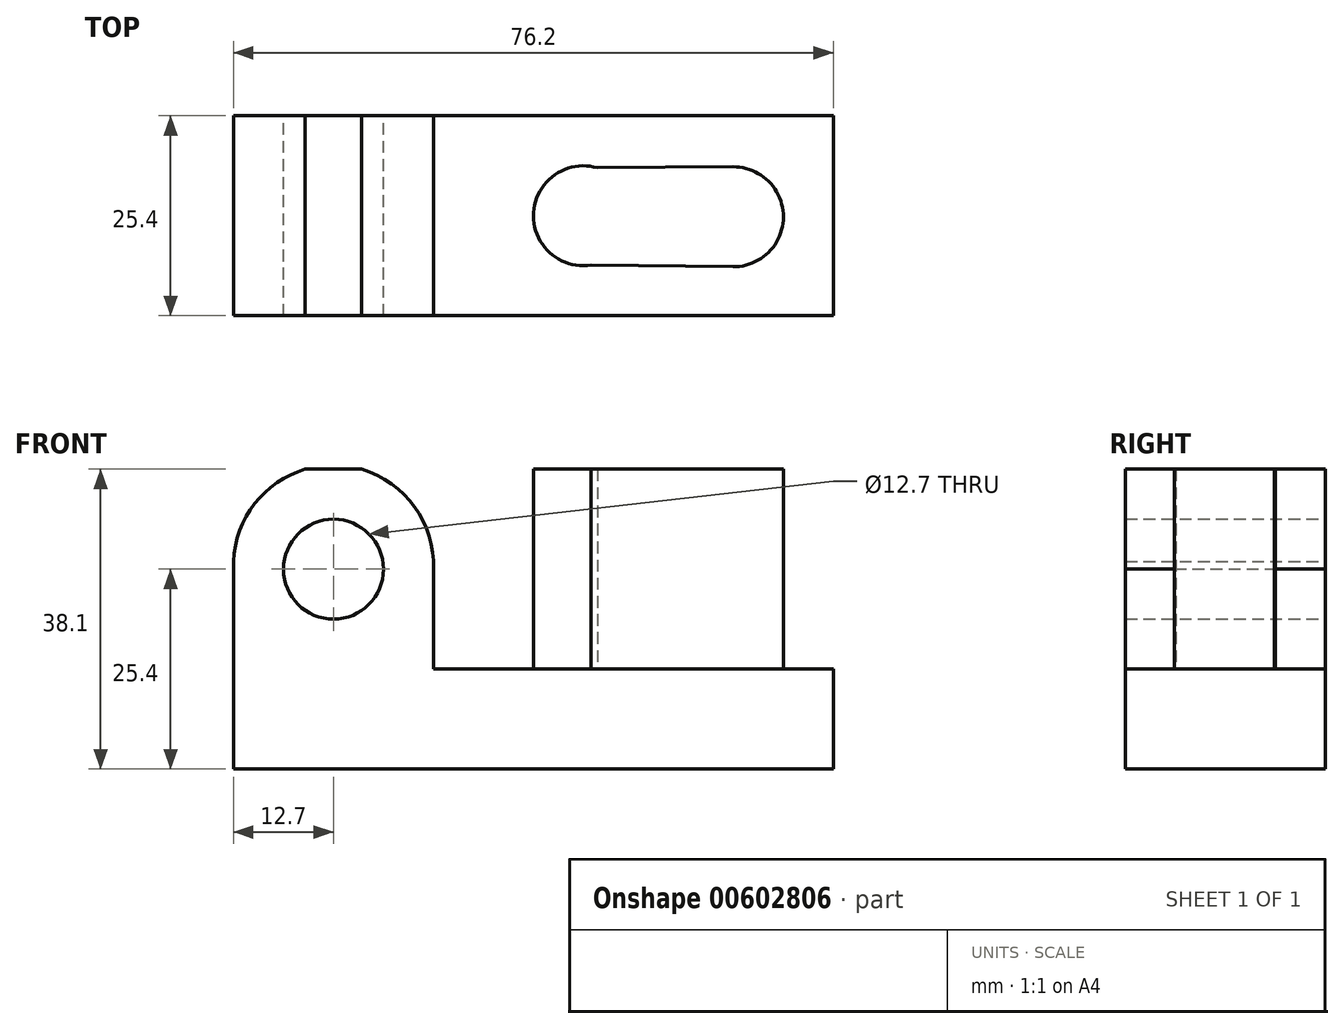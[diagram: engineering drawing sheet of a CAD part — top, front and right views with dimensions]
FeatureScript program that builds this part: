
annotation { "Feature Type Name" : "Feature", "Feature Type Description" : "" }
export const myFeature = defineFeature(function(context is Context, id is Id, definition is map)
    precondition{}
    {
        {
            var Q0;
            Q0=qCreatedBy(makeId("Front.planeOp"),FACE);
            var sketch = newSketch(context, id + "F0", { "sketchPlane" : qUnion([Q0])});
            skLineSegment(sketch, "E0", {"start": v(0, 0) * mm, "end": v(0, 38.1) * mm});
            skLineSegment(sketch, "E1", {"start": v(0, 38.1) * mm, "end": v(25.4, 38.1) * mm});
            skLineSegment(sketch, "E2", {"start": v(25.4, 38.1) * mm, "end": v(25.4, 12.7) * mm});
            skLineSegment(sketch, "E3", {"start": v(25.4, 12.7) * mm, "end": v(76.2, 12.7) * mm});
            skLineSegment(sketch, "E4", {"start": v(76.2, 12.7) * mm, "end": v(76.2, 0) * mm});
            skLineSegment(sketch, "E5", {"start": v(0, 0) * mm, "end": v(76.2, 0) * mm});
            skCircle(sketch, "E6", {"center": v(12.7, 25.4) * mm, "radius": 6.35 * mm});
            skPoint(sketch, "E6.centerSnap0", {"position": v(12.7, 38.1) * mm});
            skArc(sketch, "E7", {"start": v(25.4, 25.4) * mm, "mid": v(12.7, 38.61) * mm, "end": v(0, 25.4) * mm});
            skPoint(sketch, "E7.endSnap0", {"position": v(25.4, 25.4) * mm});
            skSolve(sketch);
        }
        {
            var Q0;
            {var subQ0=sQuery(id+"F0.wireOp",EDGE,"E7");var subQ1=sQuery(id+"F0.wireOp",EDGE,"E0");var subQ2=makeQuery(id+"F0.imprint","INTERSECT",VERTEX,{"disambiguationData":[OD(0.0)],"derivedFrom":[subQ1,subQ0]});Q0=makeQuery(id+"F0.imprint","IMPRINT",FACE,{"disambiguationData":[TD([[makeQuery(id+"F0.imprint","IMPRINT",EDGE,{"disambiguationData":[TD([[subQ2,-1.0]])],"derivedFrom":subQ1}),1.0]])]});}
            var Q1;
            {var subQ0=sQuery(id+"F0.wireOp",EDGE,"E7");var subQ1=sQuery(id+"F0.wireOp",EDGE,"E1");var subQ2=makeQuery(id+"F0.imprint","INTERSECT",VERTEX,{"disambiguationData":[OD(0.0)],"derivedFrom":[subQ1,subQ0]});Q1=makeQuery(id+"F0.imprint","IMPRINT",FACE,{"disambiguationData":[TD([[makeQuery(id+"F0.imprint","IMPRINT",EDGE,{"disambiguationData":[TD([[subQ2,-1.0]])],"derivedFrom":subQ1}),1.0]])]});}
            var Q2;
            {var subQ0=sQuery(id+"F0.wireOp",EDGE,"E7");var subQ1=sQuery(id+"F0.wireOp",EDGE,"E2");var subQ2=makeQuery(id+"F0.imprint","INTERSECT",VERTEX,{"disambiguationData":[OD(0.0)],"derivedFrom":[subQ1,subQ0]});Q2=makeQuery(id+"F0.imprint","IMPRINT",FACE,{"disambiguationData":[TD([[makeQuery(id+"F0.imprint","IMPRINT",EDGE,{"disambiguationData":[TD([[subQ2,1.0]])],"derivedFrom":subQ1}),1.0]])]});}
            var Q3;
            {var subQ5=sQuery(id+"F0.wireOp",EDGE,"E3");Q3=makeQuery(id+"F0.imprint","IMPRINT",FACE,{"disambiguationData":[TD([[makeQuery(id+"F0.imprint","IMPRINT",EDGE,{"derivedFrom":subQ5}),-1.0]])]});}
            extrude(context, id + "F1", {"entities" : qUnion([Q0, Q1, Q2, Q3]), "depth" : 25.4 * mm, "offsetDistance" : 25.4 * mm});
        }
        {
            var Q0;
            Q0=makeQuery(id+"F1.opExtrude","SWEPT_FACE",FACE,{"disambiguationData":[OSD([sQuery(id+"F0.wireOp",EDGE,"E3")])]});
            var sketch = newSketch(context, id + "F2", { "sketchPlane" : qUnion([Q0])});
            skCircle(sketch, "E8", {"center": v(44.45, -12.7) * mm, "radius": 6.35 * mm});
            skCircle(sketch, "E9", {"center": v(63.5, -12.83) * mm, "radius": 6.35 * mm});
            skLineSegment(sketch, "E10", {"start": v(46.23, -6.6) * mm, "end": v(63.46, -6.48) * mm});
            skLineSegment(sketch, "E11", {"start": v(45.4, -18.98) * mm, "end": v(63.43, -19.18) * mm});
            skSolve(sketch);
        }
        {
            var Q0;
            {var subQ0=sQuery(id+"F2.wireOp",EDGE,"E8");var subQ1=makeQuery(id+"F2.imprint","INTERSECT",VERTEX,{"derivedFrom":[subQ0,sQuery(id+"F2.wireOp",EDGE,"E10")]});Q0=makeQuery(id+"F2.imprint","IMPRINT",FACE,{"disambiguationData":[TD([[makeQuery(id+"F2.imprint","IMPRINT",EDGE,{"disambiguationData":[TD([[subQ1,-1.0]])],"derivedFrom":subQ0}),1.0]])]});}
            var Q1;
            {var subQ0=sQuery(id+"F2.wireOp",EDGE,"E9");var subQ1=makeQuery(id+"F2.imprint","INTERSECT",VERTEX,{"derivedFrom":[subQ0,sQuery(id+"F2.wireOp",EDGE,"E10")]});Q1=makeQuery(id+"F2.imprint","IMPRINT",FACE,{"disambiguationData":[TD([[makeQuery(id+"F2.imprint","IMPRINT",EDGE,{"disambiguationData":[TD([[subQ1,-1.0]])],"derivedFrom":subQ0}),1.0]])]});}
            var Q2;
            {var subQ0=sQuery(id+"F2.wireOp",EDGE,"E10");Q2=makeQuery(id+"F2.imprint","IMPRINT",FACE,{"disambiguationData":[TD([[makeQuery(id+"F2.imprint","IMPRINT",EDGE,{"derivedFrom":subQ0}),-1.0]])]});}
            extrude(context, id + "F3", {"entities" : qUnion([Q0, Q1, Q2]), "operationType" : NewBodyOperationType.ADD, "depth" : 25.4 * mm, "offsetDistance" : 25.4 * mm});
        }
    });
